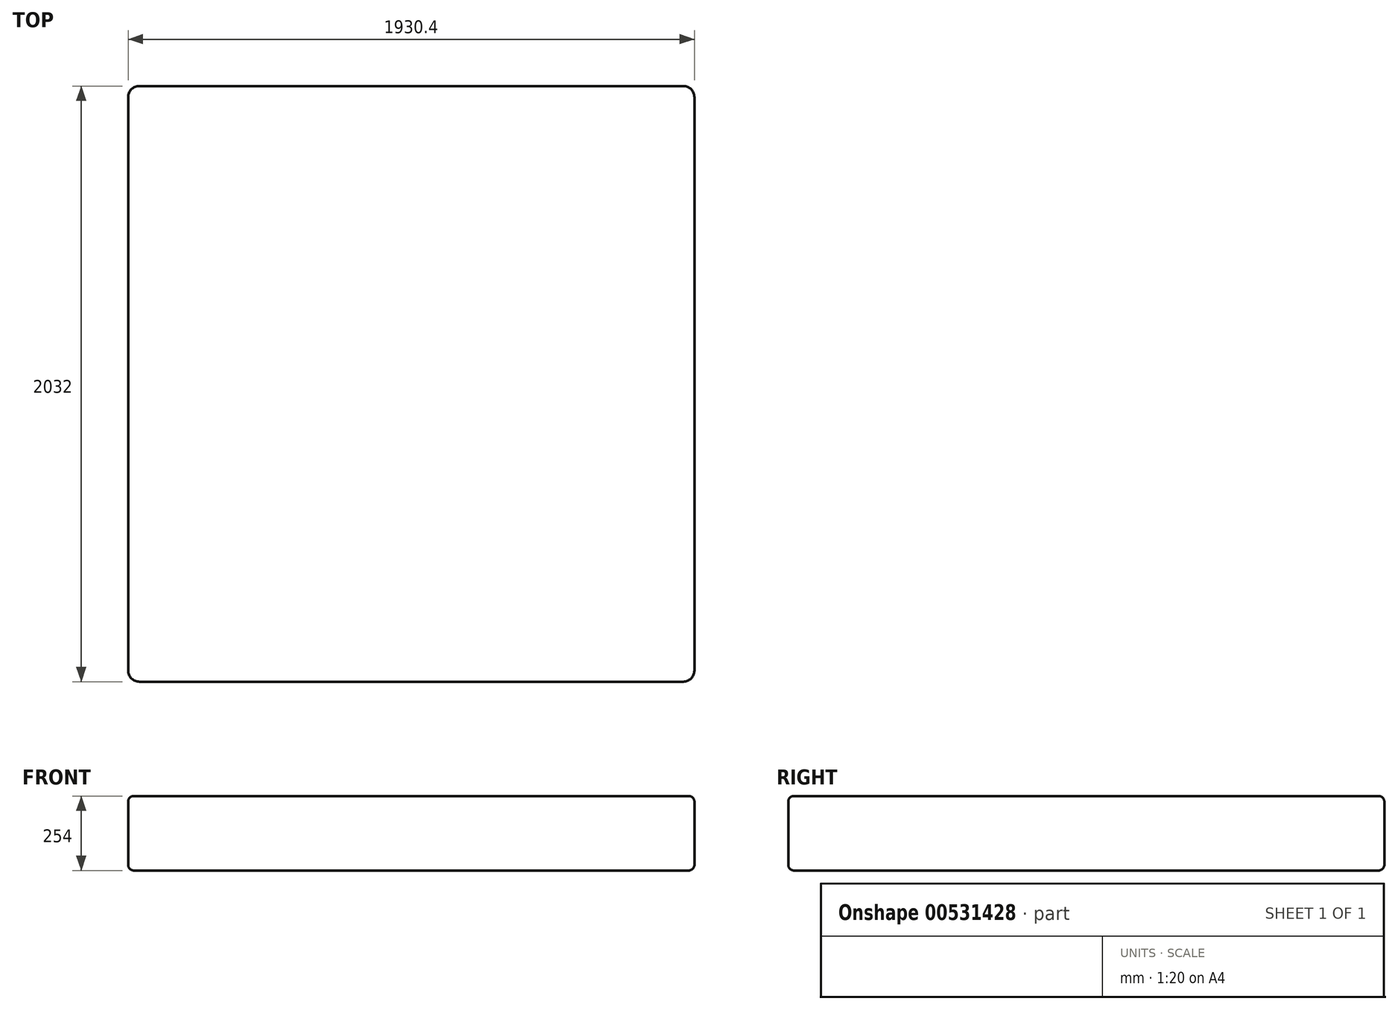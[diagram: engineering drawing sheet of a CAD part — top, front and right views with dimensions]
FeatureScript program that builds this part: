
annotation { "Feature Type Name" : "Feature", "Feature Type Description" : "" }
export const myFeature = defineFeature(function(context is Context, id is Id, definition is map)
    precondition{}
    {
        {
            assignVariable(context, id + "F0", {"name" : "MattressEdgeRadius", "anyValue" : 19.05 * mm});
        }
        {
            var Q0;
            Q0=qCreatedBy(makeId("Top.planeOp"),FACE);
            var sketch = newSketch(context, id + "F1", { "sketchPlane" : qUnion([Q0])});
            skLineSegment(sketch, "E0.bottom", {"start": v(-38.1, 0) * mm, "end": v(-1892.3, 0) * mm});
            skLineSegment(sketch, "E0.top", {"start": v(-38.1, -2032) * mm, "end": v(-1892.3, -2032) * mm});
            skLineSegment(sketch, "E0.left", {"start": v(0, -38.1) * mm, "end": v(0, -1993.9) * mm});
            skLineSegment(sketch, "E0.right", {"start": v(-1930.4, -38.1) * mm, "end": v(-1930.4, -1993.9) * mm});
            skPoint(sketch, "E1.visualSharp", {"position": v(0, 0) * mm});
            skArc(sketch, "E1.filletArc", {"start": v(0, -38.1) * mm, "mid": v(-11.16, -11.16) * mm, "end": v(-38.1, 0) * mm});
            skPoint(sketch, "E2.visualSharp", {"position": v(-1930.4, 0) * mm});
            skArc(sketch, "E2.filletArc", {"start": v(-1892.3, 0) * mm, "mid": v(-1919.24, -11.16) * mm, "end": v(-1930.4, -38.1) * mm});
            skPoint(sketch, "E3.visualSharp", {"position": v(-1930.4, -2032) * mm});
            skArc(sketch, "E3.filletArc", {"start": v(-1930.4, -1993.9) * mm, "mid": v(-1919.24, -2020.84) * mm, "end": v(-1892.3, -2032) * mm});
            skPoint(sketch, "E4.visualSharp", {"position": v(0, -2032) * mm});
            skArc(sketch, "E4.filletArc", {"start": v(-38.1, -2032) * mm, "mid": v(-11.16, -2020.84) * mm, "end": v(0, -1993.9) * mm});
            skSolve(sketch);
        }
        {
            var Q0;
            Q0=makeQuery(id+"F1.imprint","IMPRINT",FACE,{"disambiguationData":[TD([[makeQuery(id+"F1.imprint","IMPRINT",EDGE,{"derivedFrom":sQuery(id+"F1.wireOp",EDGE,"E0.bottom")}),1.0]])]});
            extrude(context, id + "F2", {"entities" : qUnion([Q0]), "depth" : 254 * mm, "offsetDistance" : 25.4 * mm});
        }
        {
            var Q0;
            Q0=makeQuery(id+"F2.opExtrude","CAP_FACE",FACE,{"disambiguationData":[OSD([sQuery(id+"F1.wireOp",EDGE,"E0.bottom"),sQuery(id+"F1.wireOp",EDGE,"E0.top"),sQuery(id+"F1.wireOp",EDGE,"E0.left"),sQuery(id+"F1.wireOp",EDGE,"E0.right"),sQuery(id+"F1.wireOp",EDGE,"E1.filletArc"),sQuery(id+"F1.wireOp",EDGE,"E2.filletArc"),sQuery(id+"F1.wireOp",EDGE,"E3.filletArc"),sQuery(id+"F1.wireOp",EDGE,"E4.filletArc")])],"isStart":false});
            fillet(context, id + "F3", {"entities" : qUnion([Q0]), "radius" : getVariable(context, 'MattressEdgeRadius'), "tangentPropagation" : true, "allowEdgeOverflow" : false});
        }
        {
            var Q0;
            Q0=makeQuery(id+"F2.opExtrude","CAP_FACE",FACE,{"disambiguationData":[OSD([sQuery(id+"F1.wireOp",EDGE,"E0.bottom"),sQuery(id+"F1.wireOp",EDGE,"E0.top"),sQuery(id+"F1.wireOp",EDGE,"E0.left"),sQuery(id+"F1.wireOp",EDGE,"E0.right"),sQuery(id+"F1.wireOp",EDGE,"E1.filletArc"),sQuery(id+"F1.wireOp",EDGE,"E2.filletArc"),sQuery(id+"F1.wireOp",EDGE,"E3.filletArc"),sQuery(id+"F1.wireOp",EDGE,"E4.filletArc")])],"isStart":true});
            fillet(context, id + "F4", {"entities" : qUnion([Q0]), "radius" : getVariable(context, 'MattressEdgeRadius'), "tangentPropagation" : true, "allowEdgeOverflow" : false});
        }
    });
